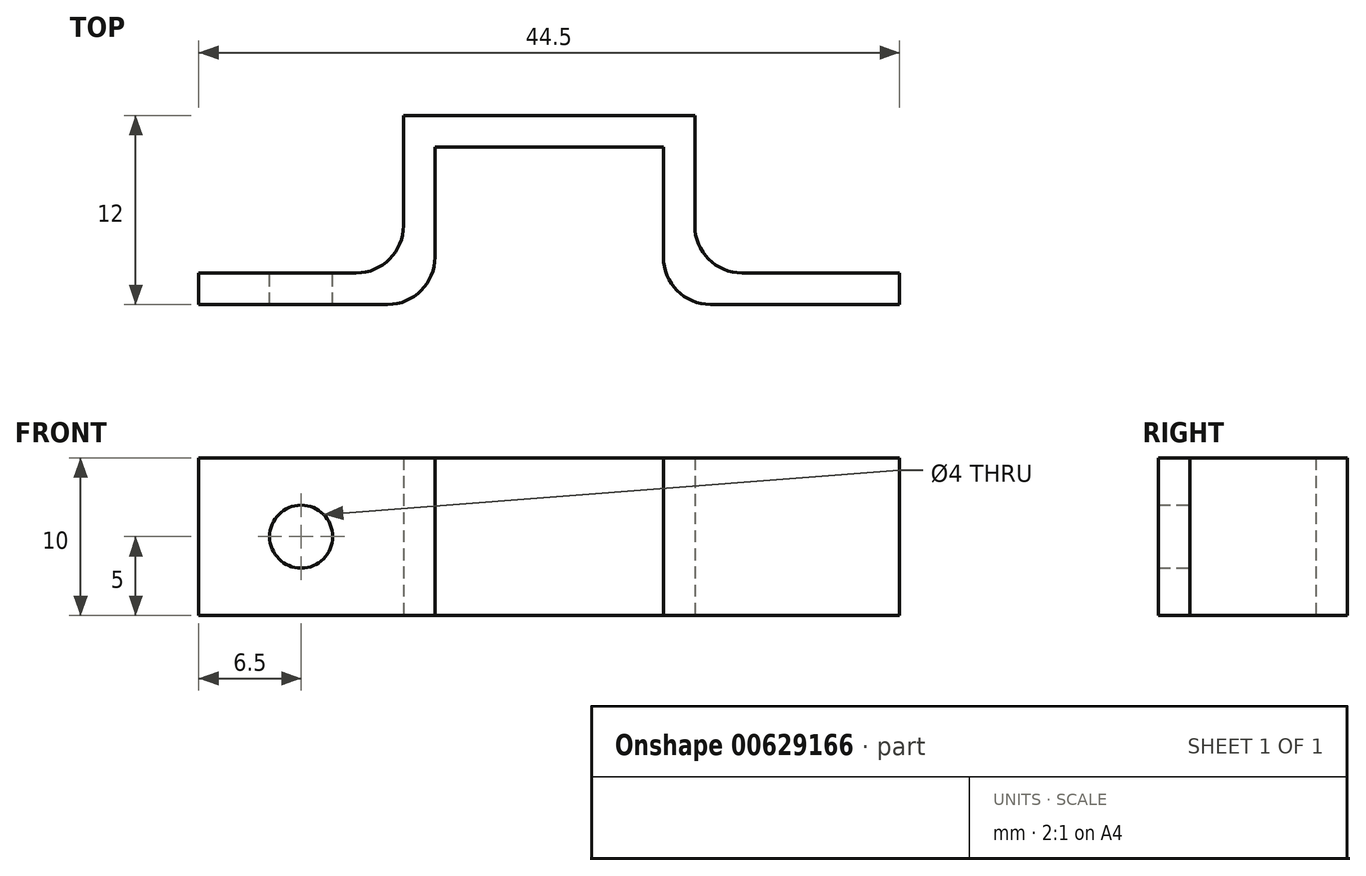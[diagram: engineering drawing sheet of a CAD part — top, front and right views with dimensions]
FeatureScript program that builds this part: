
annotation { "Feature Type Name" : "Feature", "Feature Type Description" : "" }
export const myFeature = defineFeature(function(context is Context, id is Id, definition is map)
    precondition{}
    {
        {
            var Q0;
            Q0=qCreatedBy(makeId("Top.planeOp"),FACE);
            var sketch = newSketch(context, id + "F0", { "sketchPlane" : qUnion([Q0])});
            skLineSegment(sketch, "E0", {"start": v(0, 0) * mm, "end": v(15, 0) * mm});
            skLineSegment(sketch, "E1", {"start": v(15, 0) * mm, "end": v(15, 10) * mm});
            skLineSegment(sketch, "E2", {"start": v(15, 10) * mm, "end": v(22.25, 10) * mm});
            skLineSegment(sketch, "E3", {"start": v(0, 0) * mm, "end": v(0, 2) * mm});
            skLineSegment(sketch, "E4", {"start": v(0, 2) * mm, "end": v(13, 2) * mm});
            skLineSegment(sketch, "E5", {"start": v(13, 2) * mm, "end": v(13, 12) * mm});
            skLineSegment(sketch, "E6", {"start": v(13, 12) * mm, "end": v(22.25, 12) * mm});
            skLineSegment(sketch, "E7", {"start": v(22.25, 12) * mm, "end": v(22.25, 0) * mm, "construction": true});
            skLineSegment(sketch, "E8.MirrorCS", {"start": v(44.5, 0) * mm, "end": v(44.5, 2) * mm});
            skLineSegment(sketch, "E9.MirrorCS", {"start": v(44.5, 2) * mm, "end": v(31.5, 2) * mm});
            skLineSegment(sketch, "E10.MirrorCS", {"start": v(44.5, 0) * mm, "end": v(29.5, 0) * mm});
            skLineSegment(sketch, "E11.MirrorCS", {"start": v(31.5, 2) * mm, "end": v(31.5, 12) * mm});
            skLineSegment(sketch, "E12.MirrorCS", {"start": v(29.5, 10) * mm, "end": v(22.25, 10) * mm});
            skLineSegment(sketch, "E13.MirrorCS", {"start": v(29.5, 0) * mm, "end": v(29.5, 10) * mm});
            skLineSegment(sketch, "E14.MirrorCS", {"start": v(31.5, 12) * mm, "end": v(22.25, 12) * mm});
            skSolve(sketch);
        }
        {
            var Q0;
            Q0=makeQuery(id+"F0.imprint","IMPRINT",FACE,{"disambiguationData":[TD([[makeQuery(id+"F0.imprint","IMPRINT",EDGE,{"derivedFrom":sQuery(id+"F0.wireOp",EDGE,"E0")}),1.0]])]});
            extrude(context, id + "F1", {"entities" : qUnion([Q0]), "depth" : 10 * mm, "offsetDistance" : 25 * mm});
        }
        {
            var Q0;
            Q0=makeQuery(id+"F1.opExtrude","SWEPT_FACE",FACE,{"disambiguationData":[OSD([sQuery(id+"F0.wireOp",EDGE,"E4")])]});
            var sketch = newSketch(context, id + "F2", { "sketchPlane" : qUnion([Q0])});
            skLineSegment(sketch, "E15", {"start": v(0, 5) * mm, "end": v(-13, 5) * mm, "construction": true});
            skCircle(sketch, "E16", {"center": v(-6.5, 5) * mm, "radius": 2 * mm});
            skPoint(sketch, "E17.0", {"position": v(-22.25, 10) * mm});
            skLineSegment(sketch, "E18", {"start": v(-22.25, 10) * mm, "end": v(-22.25, 0) * mm, "construction": true});
            skCircle(sketch, "E19.MirrorC", {"center": v(-38, 5) * mm, "radius": 2 * mm});
            skSolve(sketch);
        }
        {
            var Q0;
            Q0=makeQuery(id+"F2.imprint","IMPRINT",FACE,{"disambiguationData":[TD([[makeQuery(id+"F2.imprint","IMPRINT",EDGE,{"derivedFrom":sQuery(id+"F2.wireOp",EDGE,"E19.MirrorC")}),-1.0]])]});
            var Q1;
            Q1=makeQuery(id+"F2.imprint","IMPRINT",FACE,{"disambiguationData":[TD([[makeQuery(id+"F2.imprint","IMPRINT",EDGE,{"derivedFrom":sQuery(id+"F2.wireOp",EDGE,"E16")}),1.0]])]});
            extrude(context, id + "F3", {"entities" : qUnion([Q0, Q1]), "operationType" : NewBodyOperationType.REMOVE, "oppositeDirection" : true, "depth" : 25 * mm, "offsetDistance" : 25 * mm});
        }
        {
            var Q0;
            Q0=makeQuery(id+"F1.opExtrude","SWEPT_EDGE",EDGE,{"disambiguationData":[OSD([sQuery(id+"F0.wireOp",EDGE,"E9.MirrorCS"),sQuery(id+"F0.wireOp",EDGE,"E11.MirrorCS")])]});
            var Q1;
            Q1=makeQuery(id+"F1.opExtrude","SWEPT_EDGE",EDGE,{"disambiguationData":[OSD([sQuery(id+"F0.wireOp",EDGE,"E4"),sQuery(id+"F0.wireOp",EDGE,"E5")])]});
            var Q2;
            Q2=makeQuery(id+"F1.opExtrude","SWEPT_EDGE",EDGE,{"disambiguationData":[OSD([sQuery(id+"F0.wireOp",EDGE,"E10.MirrorCS"),sQuery(id+"F0.wireOp",EDGE,"E13.MirrorCS")])]});
            var Q3;
            Q3=makeQuery(id+"F1.opExtrude","SWEPT_EDGE",EDGE,{"disambiguationData":[OSD([sQuery(id+"F0.wireOp",EDGE,"E0"),sQuery(id+"F0.wireOp",EDGE,"E1")])]});
            fillet(context, id + "F4", {"entities" : qUnion([Q0, Q1, Q2, Q3]), "radius" : 3 * mm, "tangentPropagation" : true, "allowEdgeOverflow" : false});
        }
    });
